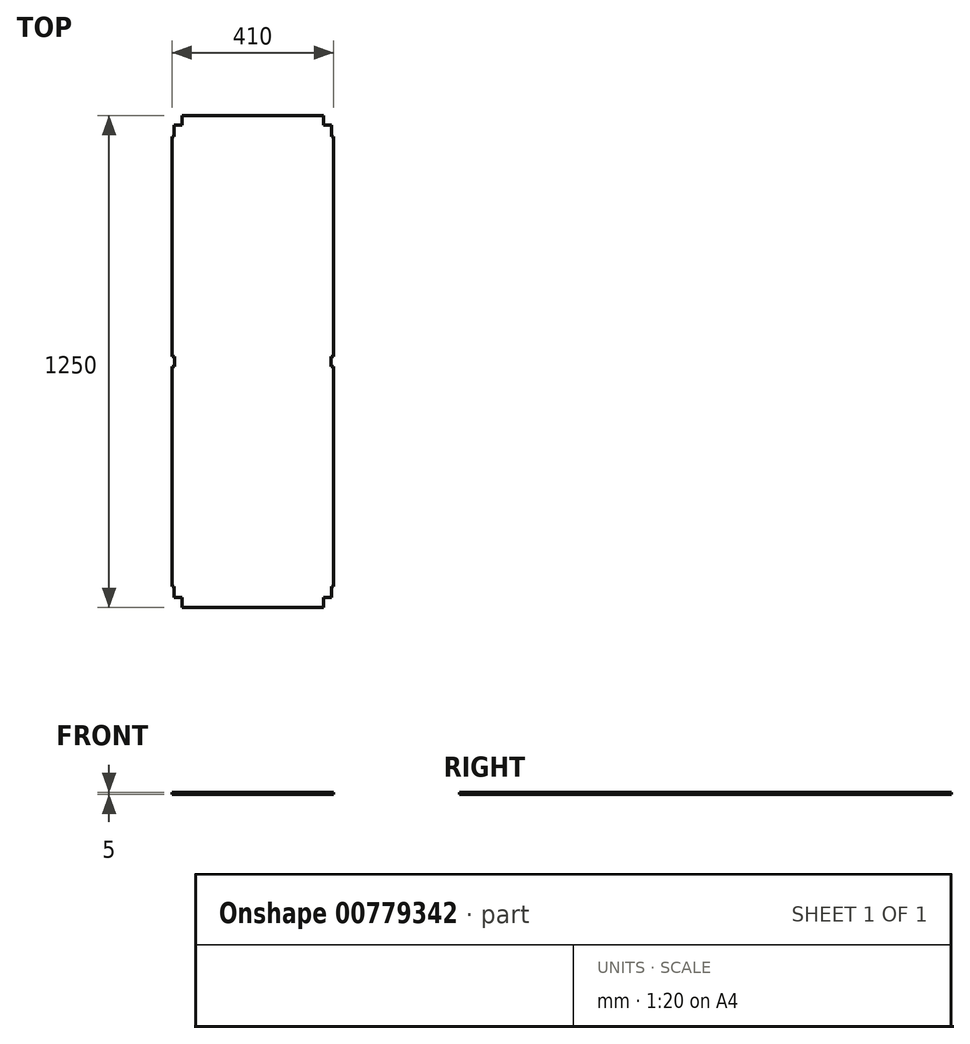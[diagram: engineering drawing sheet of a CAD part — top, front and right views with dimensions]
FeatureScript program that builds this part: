
annotation { "Feature Type Name" : "Feature", "Feature Type Description" : "" }
export const myFeature = defineFeature(function(context is Context, id is Id, definition is map)
    precondition{}
    {
        {
            var Q0;
            Q0=qCreatedBy(makeId("Top.planeOp"),FACE);
            var sketch = newSketch(context, id + "F0", { "sketchPlane" : qUnion([Q0])});
            skLineSegment(sketch, "E0.bottom", {"start": v(0, 0) * mm, "end": v(410, 0) * mm});
            skLineSegment(sketch, "E0.top", {"start": v(0, 1250) * mm, "end": v(410, 1250) * mm});
            skLineSegment(sketch, "E0.left", {"start": v(0, 0) * mm, "end": v(0, 1250) * mm});
            skLineSegment(sketch, "E0.right", {"start": v(410, 0) * mm, "end": v(410, 1250) * mm});
            skSolve(sketch);
        }
        {
            var Q0;
            Q0=qSketchRegion(id+"F0",true);
            extrude(context, id + "F1", {"entities" : qUnion([Q0]), "depth" : 5 * mm});
        }
        {
            var Q0;
            Q0=makeQuery(id+"F1.opExtrude","CAP_FACE",FACE,{"disambiguationData":[OSD([sQuery(id+"F0.wireOp",EDGE,"E0.bottom"),sQuery(id+"F0.wireOp",EDGE,"E0.top"),sQuery(id+"F0.wireOp",EDGE,"E0.left"),sQuery(id+"F0.wireOp",EDGE,"E0.right")])],"isStart":false});
            var sketch = newSketch(context, id + "F2", { "sketchPlane" : qUnion([Q0])});
            skLineSegment(sketch, "E1.bottom", {"start": v(0, 0) * mm, "end": v(25, 0) * mm});
            skLineSegment(sketch, "E1.top", {"start": v(0, 25) * mm, "end": v(25, 25) * mm});
            skLineSegment(sketch, "E1.left", {"start": v(0, 0) * mm, "end": v(0, 25) * mm});
            skLineSegment(sketch, "E1.right", {"start": v(25, 0) * mm, "end": v(25, 25) * mm});
            skSolve(sketch);
        }
        {
            var Q0;
            Q0=qSketchRegion(id+"F2",true);
            extrude(context, id + "F3", {"entities" : qUnion([Q0]), "operationType" : NewBodyOperationType.REMOVE, "oppositeDirection" : true, "depth" : 25 * mm});
        }
        {
            var Q0;
            Q0=makeQuery(id+"F1.opExtrude","CAP_FACE",FACE,{"disambiguationData":[OSD([sQuery(id+"F0.wireOp",EDGE,"E0.bottom"),sQuery(id+"F0.wireOp",EDGE,"E0.top"),sQuery(id+"F0.wireOp",EDGE,"E0.left"),sQuery(id+"F0.wireOp",EDGE,"E0.right")])],"isStart":false});
            var sketch = newSketch(context, id + "F4", { "sketchPlane" : qUnion([Q0])});
            skLineSegment(sketch, "E2.bottom", {"start": v(410, 0) * mm, "end": v(385, 0) * mm});
            skLineSegment(sketch, "E2.top", {"start": v(410, 25) * mm, "end": v(385, 25) * mm});
            skLineSegment(sketch, "E2.left", {"start": v(410, 0) * mm, "end": v(410, 25) * mm});
            skLineSegment(sketch, "E2.right", {"start": v(385, 0) * mm, "end": v(385, 25) * mm});
            skSolve(sketch);
        }
        {
            var Q0;
            Q0=qSketchRegion(id+"F4",true);
            extrude(context, id + "F5", {"entities" : qUnion([Q0]), "operationType" : NewBodyOperationType.REMOVE, "oppositeDirection" : true, "depth" : 25 * mm});
        }
        {
            var Q0;
            Q0=makeQuery(id+"F1.opExtrude","CAP_FACE",FACE,{"disambiguationData":[OSD([sQuery(id+"F0.wireOp",EDGE,"E0.bottom"),sQuery(id+"F0.wireOp",EDGE,"E0.top"),sQuery(id+"F0.wireOp",EDGE,"E0.left"),sQuery(id+"F0.wireOp",EDGE,"E0.right")])],"isStart":false});
            var sketch = newSketch(context, id + "F6", { "sketchPlane" : qUnion([Q0])});
            skLineSegment(sketch, "E3.bottom", {"start": v(410, 1250) * mm, "end": v(385, 1250) * mm});
            skLineSegment(sketch, "E3.top", {"start": v(410, 1225) * mm, "end": v(385, 1225) * mm});
            skLineSegment(sketch, "E3.left", {"start": v(410, 1250) * mm, "end": v(410, 1225) * mm});
            skLineSegment(sketch, "E3.right", {"start": v(385, 1250) * mm, "end": v(385, 1225) * mm});
            skSolve(sketch);
        }
        {
            var Q0;
            Q0=qSketchRegion(id+"F6",true);
            extrude(context, id + "F7", {"entities" : qUnion([Q0]), "operationType" : NewBodyOperationType.REMOVE, "oppositeDirection" : true, "depth" : 25 * mm});
        }
        {
            var Q0;
            Q0=makeQuery(id+"F1.opExtrude","CAP_FACE",FACE,{"disambiguationData":[OSD([sQuery(id+"F0.wireOp",EDGE,"E0.bottom"),sQuery(id+"F0.wireOp",EDGE,"E0.top"),sQuery(id+"F0.wireOp",EDGE,"E0.left"),sQuery(id+"F0.wireOp",EDGE,"E0.right")])],"isStart":false});
            var sketch = newSketch(context, id + "F8", { "sketchPlane" : qUnion([Q0])});
            skLineSegment(sketch, "E4.bottom", {"start": v(0, 1250) * mm, "end": v(25, 1250) * mm});
            skLineSegment(sketch, "E4.top", {"start": v(0, 1225) * mm, "end": v(25, 1225) * mm});
            skLineSegment(sketch, "E4.left", {"start": v(0, 1250) * mm, "end": v(0, 1225) * mm});
            skLineSegment(sketch, "E4.right", {"start": v(25, 1250) * mm, "end": v(25, 1225) * mm});
            skSolve(sketch);
        }
        {
            var Q0;
            Q0=makeQuery(id+"F8.imprint","IMPRINT",FACE,{"disambiguationData":[TD([[makeQuery(id+"F8.imprint","IMPRINT",EDGE,{"derivedFrom":sQuery(id+"F8.wireOp",EDGE,"E4.bottom")}),-1.0]])]});
            extrude(context, id + "F9", {"entities" : qUnion([Q0]), "operationType" : NewBodyOperationType.REMOVE, "oppositeDirection" : true, "depth" : 25 * mm});
        }
        {
            var Q0;
            Q0=makeQuery(id+"F1.opExtrude","CAP_FACE",FACE,{"disambiguationData":[OSD([sQuery(id+"F0.wireOp",EDGE,"E0.bottom"),sQuery(id+"F0.wireOp",EDGE,"E0.top"),sQuery(id+"F0.wireOp",EDGE,"E0.left"),sQuery(id+"F0.wireOp",EDGE,"E0.right")])],"isStart":false});
            var sketch = newSketch(context, id + "F10", { "sketchPlane" : qUnion([Q0])});
            skLineSegment(sketch, "E5.bottom", {"start": v(6, 638) * mm, "end": v(-6, 638) * mm});
            skLineSegment(sketch, "E5.top", {"start": v(6, 612) * mm, "end": v(-6, 612) * mm});
            skLineSegment(sketch, "E5.left", {"start": v(-6, 638) * mm, "end": v(-6, 612) * mm});
            skLineSegment(sketch, "E5.right", {"start": v(6, 638) * mm, "end": v(6, 612) * mm});
            skPoint(sketch, "E5.middle", {"position": v(0, 625) * mm});
            skSolve(sketch);
        }
        {
            var Q0;
            Q0=qSketchRegion(id+"F10",true);
            extrude(context, id + "F11", {"entities" : qUnion([Q0]), "operationType" : NewBodyOperationType.REMOVE, "oppositeDirection" : true, "depth" : 25 * mm});
        }
        {
            var Q0;
            Q0=makeQuery(id+"F1.opExtrude","CAP_FACE",FACE,{"disambiguationData":[OSD([sQuery(id+"F0.wireOp",EDGE,"E0.bottom"),sQuery(id+"F0.wireOp",EDGE,"E0.top"),sQuery(id+"F0.wireOp",EDGE,"E0.left"),sQuery(id+"F0.wireOp",EDGE,"E0.right")])],"isStart":false});
            var sketch = newSketch(context, id + "F12", { "sketchPlane" : qUnion([Q0])});
            skLineSegment(sketch, "E6.bottom", {"start": v(404, 638) * mm, "end": v(416, 638) * mm});
            skLineSegment(sketch, "E6.top", {"start": v(404, 612) * mm, "end": v(416, 612) * mm});
            skLineSegment(sketch, "E6.left", {"start": v(404, 638) * mm, "end": v(404, 612) * mm});
            skLineSegment(sketch, "E6.right", {"start": v(416, 638) * mm, "end": v(416, 612) * mm});
            skPoint(sketch, "E6.middle", {"position": v(410, 625) * mm});
            skSolve(sketch);
        }
        {
            var Q0;
            Q0=qSketchRegion(id+"F12",true);
            extrude(context, id + "F13", {"entities" : qUnion([Q0]), "operationType" : NewBodyOperationType.REMOVE, "oppositeDirection" : true, "depth" : 25 * mm});
        }
        {
            var Q0;
            Q0=makeQuery(id+"F1.opExtrude","CAP_FACE",FACE,{"disambiguationData":[OSD([sQuery(id+"F0.wireOp",EDGE,"E0.bottom"),sQuery(id+"F0.wireOp",EDGE,"E0.top"),sQuery(id+"F0.wireOp",EDGE,"E0.left"),sQuery(id+"F0.wireOp",EDGE,"E0.right")])],"isStart":false});
            var sketch = newSketch(context, id + "F14", { "sketchPlane" : qUnion([Q0])});
            skLineSegment(sketch, "E7.bottom", {"start": v(410, 25) * mm, "end": v(405, 25) * mm});
            skLineSegment(sketch, "E7.top", {"start": v(410, 53) * mm, "end": v(405, 53) * mm});
            skLineSegment(sketch, "E7.left", {"start": v(410, 25) * mm, "end": v(410, 53) * mm});
            skLineSegment(sketch, "E7.right", {"start": v(405, 25) * mm, "end": v(405, 53) * mm});
            skSolve(sketch);
        }
        {
            var Q0;
            Q0=qSketchRegion(id+"F14",true);
            extrude(context, id + "F15", {"entities" : qUnion([Q0]), "operationType" : NewBodyOperationType.REMOVE, "oppositeDirection" : true, "depth" : 25 * mm});
        }
        {
            var Q0;
            Q0=makeQuery(id+"F1.opExtrude","CAP_FACE",FACE,{"disambiguationData":[OSD([sQuery(id+"F0.wireOp",EDGE,"E0.bottom"),sQuery(id+"F0.wireOp",EDGE,"E0.top"),sQuery(id+"F0.wireOp",EDGE,"E0.left"),sQuery(id+"F0.wireOp",EDGE,"E0.right")])],"isStart":false});
            var sketch = newSketch(context, id + "F16", { "sketchPlane" : qUnion([Q0])});
            skLineSegment(sketch, "E8.bottom", {"start": v(410, 1225) * mm, "end": v(405, 1225) * mm});
            skLineSegment(sketch, "E8.top", {"start": v(410, 1197) * mm, "end": v(405, 1197) * mm});
            skLineSegment(sketch, "E8.left", {"start": v(410, 1225) * mm, "end": v(410, 1197) * mm});
            skLineSegment(sketch, "E8.right", {"start": v(405, 1225) * mm, "end": v(405, 1197) * mm});
            skSolve(sketch);
        }
        {
            var Q0;
            Q0=qSketchRegion(id+"F16",true);
            extrude(context, id + "F17", {"entities" : qUnion([Q0]), "operationType" : NewBodyOperationType.REMOVE, "oppositeDirection" : true, "depth" : 25 * mm});
        }
        {
            var Q0;
            Q0=makeQuery(id+"F1.opExtrude","CAP_FACE",FACE,{"disambiguationData":[OSD([sQuery(id+"F0.wireOp",EDGE,"E0.bottom"),sQuery(id+"F0.wireOp",EDGE,"E0.top"),sQuery(id+"F0.wireOp",EDGE,"E0.left"),sQuery(id+"F0.wireOp",EDGE,"E0.right")])],"isStart":false});
            var sketch = newSketch(context, id + "F18", { "sketchPlane" : qUnion([Q0])});
            skLineSegment(sketch, "E9.bottom", {"start": v(0, 1225) * mm, "end": v(5, 1225) * mm});
            skLineSegment(sketch, "E9.top", {"start": v(0, 1197) * mm, "end": v(5, 1197) * mm});
            skLineSegment(sketch, "E9.left", {"start": v(0, 1225) * mm, "end": v(0, 1197) * mm});
            skLineSegment(sketch, "E9.right", {"start": v(5, 1225) * mm, "end": v(5, 1197) * mm});
            skSolve(sketch);
        }
        {
            var Q0;
            Q0=qSketchRegion(id+"F18",true);
            extrude(context, id + "F19", {"entities" : qUnion([Q0]), "operationType" : NewBodyOperationType.REMOVE, "oppositeDirection" : true, "depth" : 25 * mm});
        }
        {
            var Q0;
            Q0=makeQuery(id+"F1.opExtrude","CAP_FACE",FACE,{"disambiguationData":[OSD([sQuery(id+"F0.wireOp",EDGE,"E0.bottom"),sQuery(id+"F0.wireOp",EDGE,"E0.top"),sQuery(id+"F0.wireOp",EDGE,"E0.left"),sQuery(id+"F0.wireOp",EDGE,"E0.right")])],"isStart":false});
            var sketch = newSketch(context, id + "F20", { "sketchPlane" : qUnion([Q0])});
            skLineSegment(sketch, "E10.bottom", {"start": v(0, 25) * mm, "end": v(5, 25) * mm});
            skLineSegment(sketch, "E10.top", {"start": v(0, 53) * mm, "end": v(5, 53) * mm});
            skLineSegment(sketch, "E10.left", {"start": v(0, 25) * mm, "end": v(0, 53) * mm});
            skLineSegment(sketch, "E10.right", {"start": v(5, 25) * mm, "end": v(5, 53) * mm});
            skSolve(sketch);
        }
        {
            var Q0;
            Q0=qSketchRegion(id+"F20",true);
            extrude(context, id + "F21", {"entities" : qUnion([Q0]), "operationType" : NewBodyOperationType.REMOVE, "oppositeDirection" : true, "depth" : 25 * mm});
        }
    });
